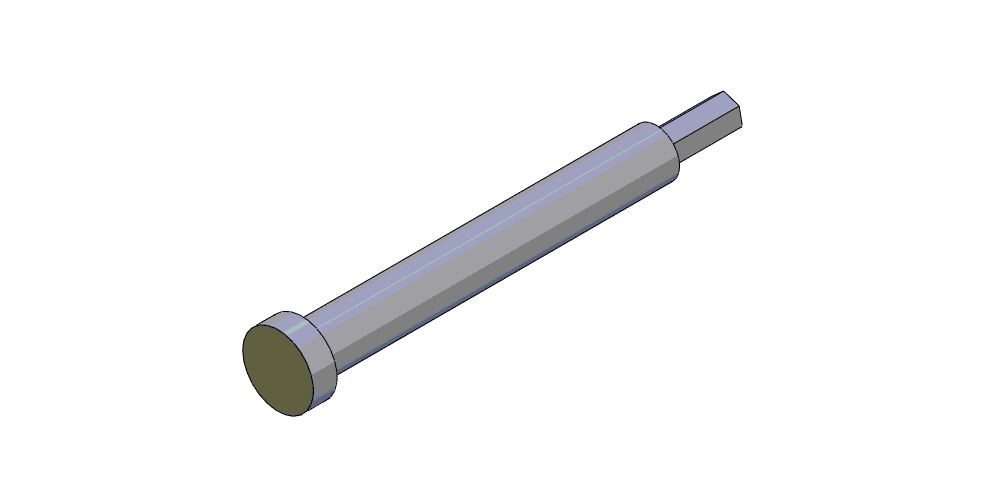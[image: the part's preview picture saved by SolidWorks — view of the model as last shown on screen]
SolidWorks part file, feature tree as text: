
SOLIDWORKS PART (.sldprt)
format: sldprt  version: not decoded by parser v0  size: 133,632 bytes
history: native  units: mm
features: plane x3, sketch x3, extrude x3, material x1 (+9 scaffold rows collapsed)
feature tree (19):
  scaffold x9  (default folders/planes/origin — collapsed)
  material  "Matériau <non spécifié>"
  plane  "Plan de face"
  plane  "Plan de dessus"
  plane  "Plan de droite"
  sketch  "Esquisse1"  dims[D1=6.0mm]
  extrude  "Boss.-Extru.1"  Depth=15mm
  sketch  "Esquisse2"  dims[D1=10.0mm]
  extrude  "Boss.-Extru.2"  Depth=75mm
  sketch  "Esquisse3"  dims[D1=15.0mm]
  extrude  "Boss.-Extru.3"  Depth=5mm
decode coverage: 6 of 6 modeling features carry decoded parameters
note: suppression state not decoded; provenance and decode notes live in map.json
